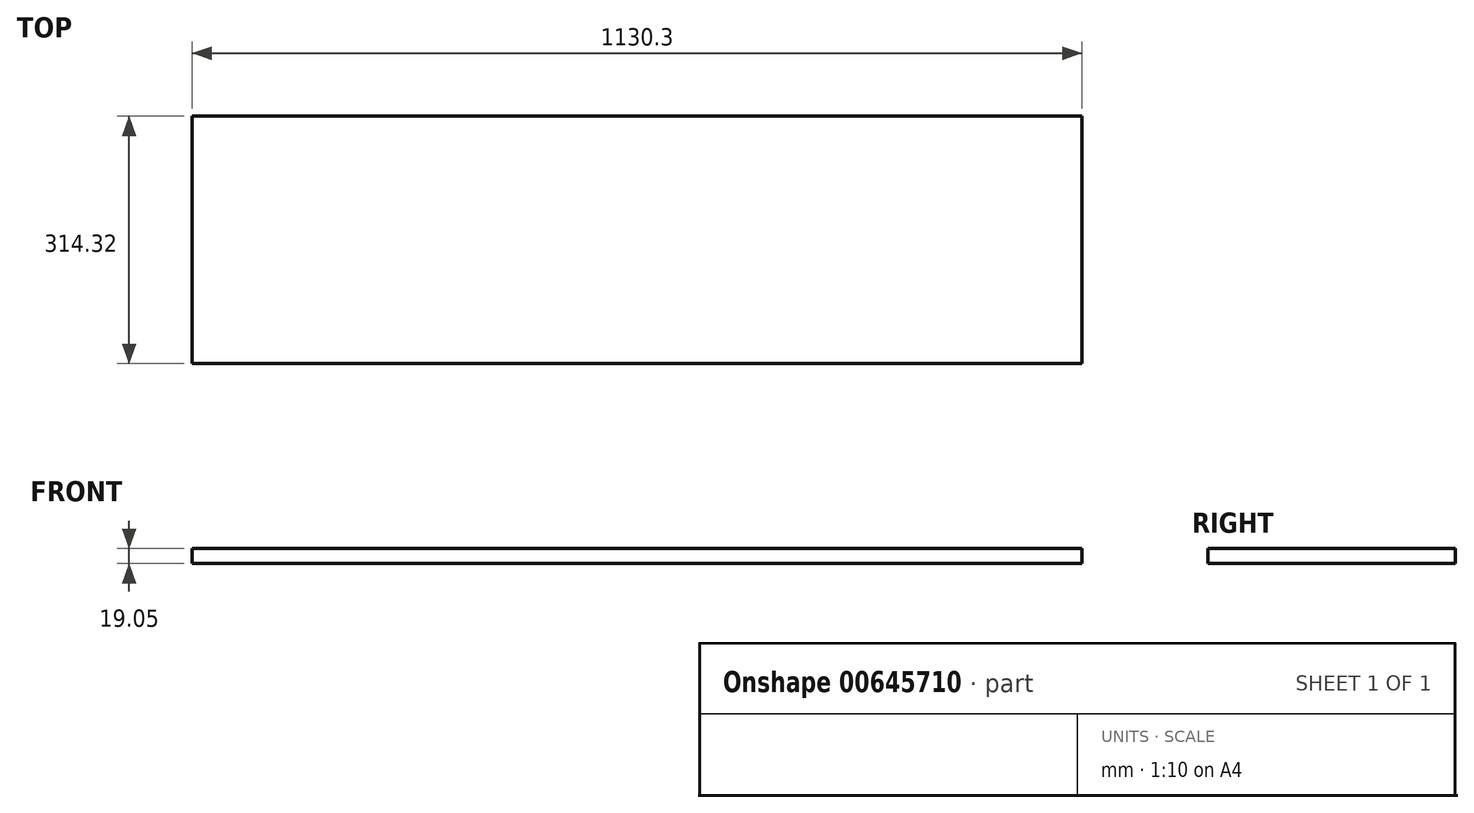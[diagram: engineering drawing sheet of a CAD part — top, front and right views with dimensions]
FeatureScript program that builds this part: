
annotation { "Feature Type Name" : "Feature", "Feature Type Description" : "" }
export const myFeature = defineFeature(function(context is Context, id is Id, definition is map)
    precondition{}
    {
        {
            var Q0;
            Q0=qCreatedBy(makeId("Top.planeOp"),FACE);
            var sketch = newSketch(context, id + "F0", { "sketchPlane" : qUnion([Q0])});
            skLineSegment(sketch, "E0.bottom", {"start": v(565.15, 157.16) * mm, "end": v(-565.15, 157.16) * mm});
            skLineSegment(sketch, "E0.top", {"start": v(565.15, -157.16) * mm, "end": v(-565.15, -157.16) * mm});
            skLineSegment(sketch, "E0.left", {"start": v(565.15, 157.16) * mm, "end": v(565.15, -157.16) * mm});
            skLineSegment(sketch, "E0.right", {"start": v(-565.15, 157.16) * mm, "end": v(-565.15, -157.16) * mm});
            skPoint(sketch, "E0.middle", {"position": v(0, 0) * mm});
            skSolve(sketch);
        }
        {
            var Q0;
            Q0=makeQuery(id+"F0.imprint","IMPRINT",FACE,{"disambiguationData":[TD([[makeQuery(id+"F0.imprint","IMPRINT",EDGE,{"derivedFrom":sQuery(id+"F0.wireOp",EDGE,"E0.bottom")}),1.0]])]});
            extrude(context, id + "F1", {"entities" : qUnion([Q0]), "depth" : 19.05 * mm, "offsetDistance" : 25.4 * mm});
        }
    });
